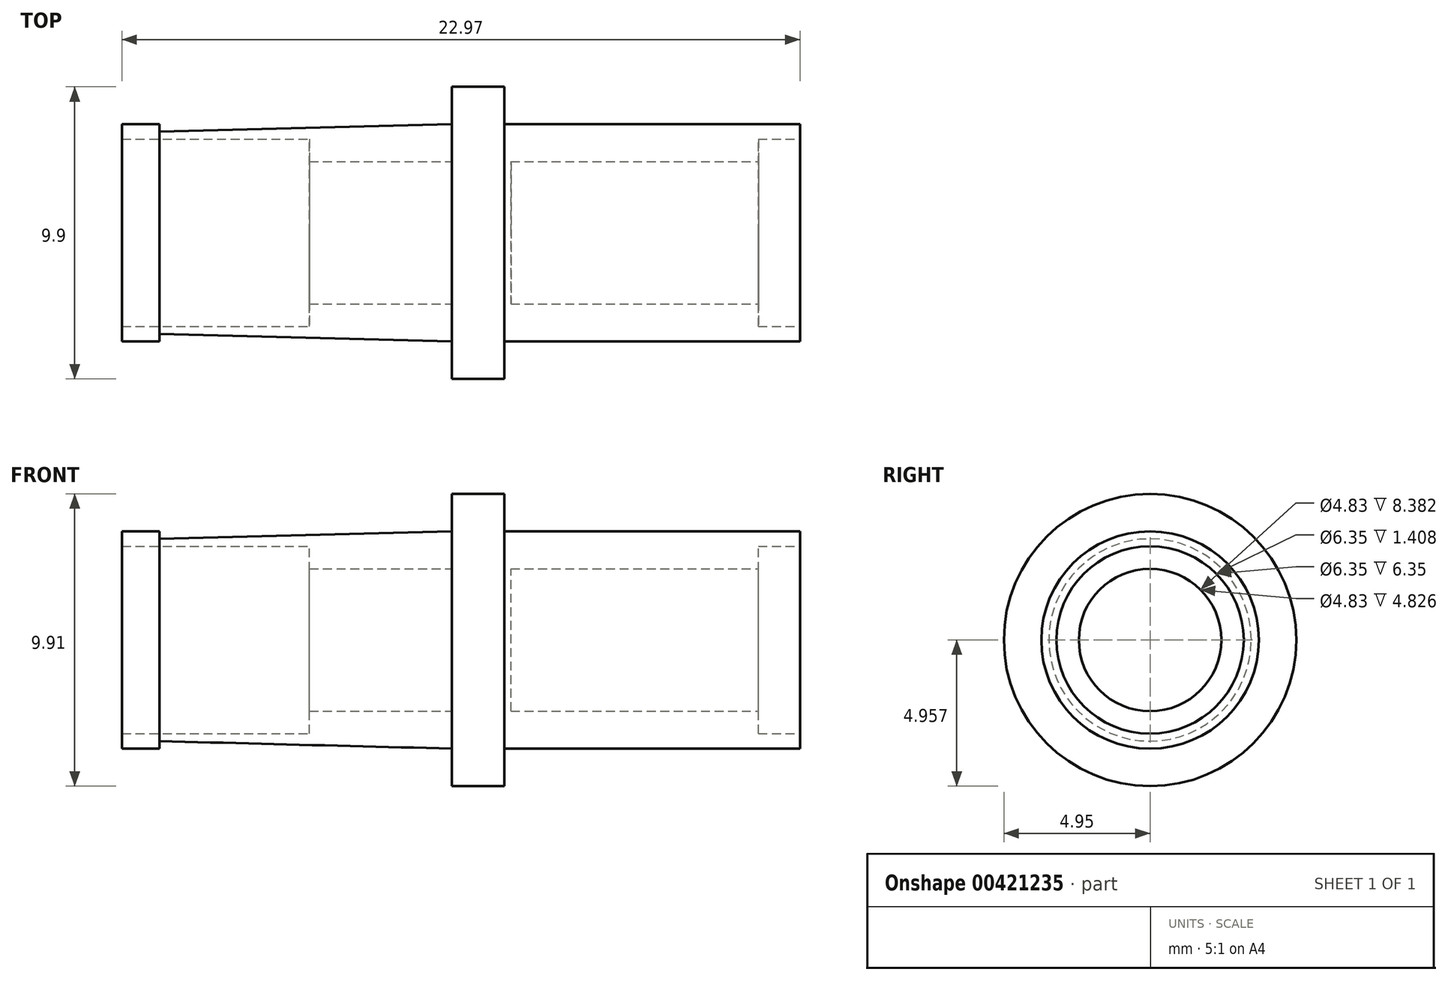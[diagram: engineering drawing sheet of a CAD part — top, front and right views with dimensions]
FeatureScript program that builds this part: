
annotation { "Feature Type Name" : "Feature", "Feature Type Description" : "" }
export const myFeature = defineFeature(function(context is Context, id is Id, definition is map)
    precondition{}
    {
        {
            var Q0;
            Q0=qCreatedBy(makeId("Front.planeOp"),FACE);
            var sketch = newSketch(context, id + "F0", { "sketchPlane" : qUnion([Q0])});
            skLineSegment(sketch, "E0", {"start": v(0, 0) * mm, "end": v(0, 1.27) * mm});
            skLineSegment(sketch, "E1", {"start": v(0, 1.27) * mm, "end": v(1.78, 1.27) * mm});
            skLineSegment(sketch, "E2", {"start": v(1.78, 1.27) * mm, "end": v(1.78, 0) * mm});
            skLineSegment(sketch, "E3", {"start": v(1.78, 0) * mm, "end": v(11.79, 0) * mm});
            skLineSegment(sketch, "E4", {"start": v(11.79, 0) * mm, "end": v(11.79, -0.5) * mm});
            skLineSegment(sketch, "E5", {"start": v(11.79, -0.5) * mm, "end": v(10.38, -0.5) * mm});
            skLineSegment(sketch, "E6", {"start": v(10.38, -0.5) * mm, "end": v(10.38, -1.27) * mm});
            skLineSegment(sketch, "E7", {"start": v(10.38, -1.27) * mm, "end": v(2, -1.27) * mm});
            skLineSegment(sketch, "E8", {"start": v(2, -1.27) * mm, "end": v(2, -3.68) * mm});
            skLineSegment(sketch, "E9", {"start": v(2, -3.68) * mm, "end": v(0, -3.68) * mm});
            skLineSegment(sketch, "E10", {"start": v(0, -3.68) * mm, "end": v(0, -1.27) * mm});
            skLineSegment(sketch, "E11", {"start": v(0, -1.27) * mm, "end": v(-4.83, -1.27) * mm});
            skLineSegment(sketch, "E12", {"start": v(-4.83, -1.27) * mm, "end": v(-4.83, -0.5) * mm});
            skLineSegment(sketch, "E13", {"start": v(-4.83, -0.5) * mm, "end": v(-11.18, -0.5) * mm});
            skLineSegment(sketch, "E14", {"start": v(-11.18, -0.5) * mm, "end": v(-11.18, 0) * mm});
            skLineSegment(sketch, "E15", {"start": v(-11.18, 0) * mm, "end": v(-9.9, 0) * mm});
            skLineSegment(sketch, "E16", {"start": v(-9.9, 0) * mm, "end": v(-9.9, -0.25) * mm});
            skLineSegment(sketch, "E17", {"start": v(-9.9, -0.25) * mm, "end": v(0, 0) * mm});
            skLineSegment(sketch, "E18", {"start": v(12.79, -3.68) * mm, "end": v(-14.22, -3.68) * mm});
            skSolve(sketch);
        }
        {
            var Q0;
            Q0=makeQuery(id+"F0.imprint","IMPRINT",FACE,{"disambiguationData":[TD([[makeQuery(id+"F0.imprint","IMPRINT",EDGE,{"derivedFrom":sQuery(id+"F0.wireOp",EDGE,"E0")}),-1.0]])]});
            var Q1;
            Q1=sQuery(id+"F0.wireOp",EDGE,"E18");
            revolve(context, id + "F1", {"entities" : qUnion([Q0]), "axis" : qUnion([Q1]), "revolveType" : RevolveType.FULL});
        }
    });
